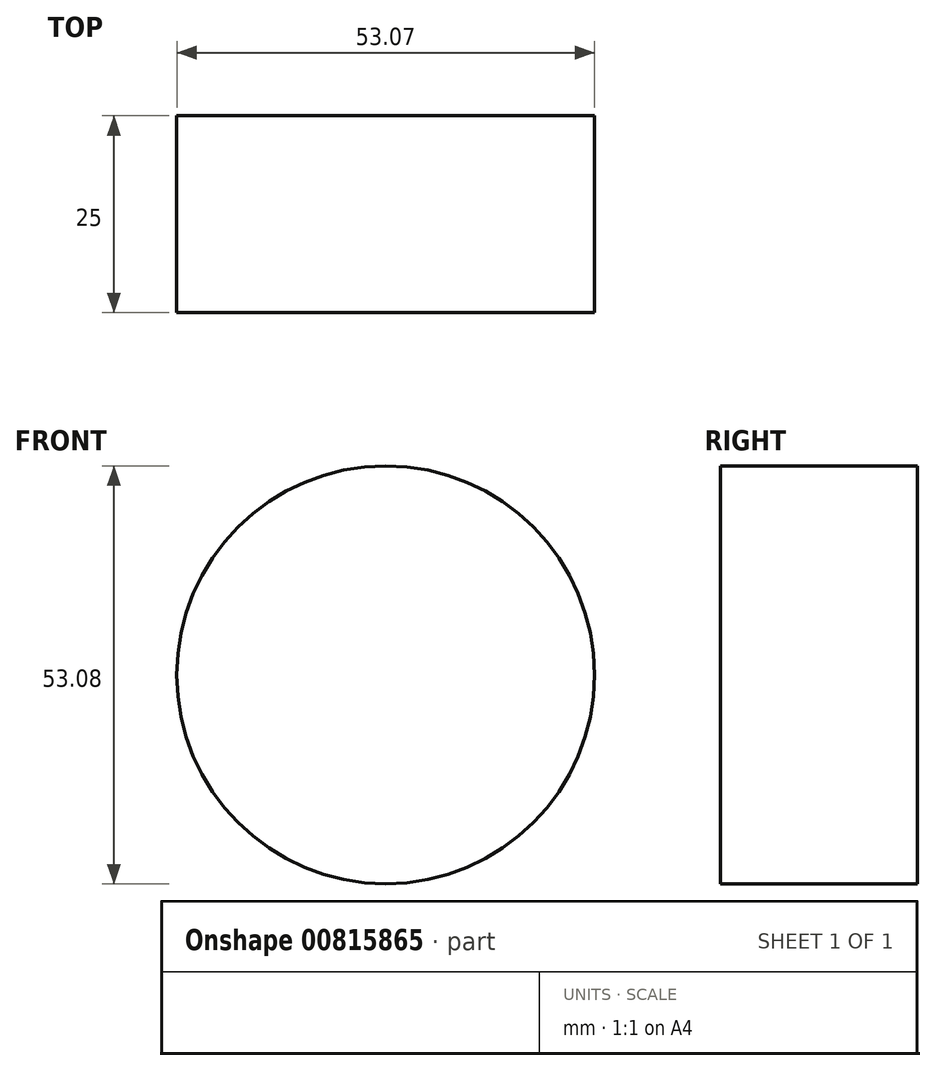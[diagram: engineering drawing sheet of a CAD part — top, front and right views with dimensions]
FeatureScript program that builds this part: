
annotation { "Feature Type Name" : "Feature", "Feature Type Description" : "" }
export const myFeature = defineFeature(function(context is Context, id is Id, definition is map)
    precondition{}
    {
        {
            var Q0;
            Q0=qCreatedBy(makeId("Front.planeOp"),FACE);
            var sketch = newSketch(context, id + "F0", { "sketchPlane" : qUnion([Q0])});
            skLineSegment(sketch, "E0.bottom", {"start": v(-136.5, 52.24) * mm, "end": v(-70.13, 52.24) * mm});
            skLineSegment(sketch, "E0.top", {"start": v(-136.5, 0) * mm, "end": v(-70.13, 0) * mm});
            skLineSegment(sketch, "E0.left", {"start": v(-136.5, 52.24) * mm, "end": v(-136.5, 0) * mm});
            skLineSegment(sketch, "E0.right", {"start": v(-70.13, 52.24) * mm, "end": v(-70.13, 0) * mm});
            skCircle(sketch, "E1", {"center": v(45.03, 64.32) * mm, "radius": 26.54 * mm});
            skSolve(sketch);
        }
        {
            var Q0;
            Q0 = qSketchRegion(id + "F0", true);
            extrude(context, id + "F1", {"entities" : qUnion([Q0]), "depth" : 25 * mm, "offsetDistance" : 25 * mm});
        }
        {
            var Q0;
            Q0=makeQuery(id+"F1.opExtrude","SWEPT_BODY",BODY,{"disambiguationData":[OSD([sQuery(id+"F0.wireOp",EDGE,"E0.bottom"),sQuery(id+"F0.wireOp",EDGE,"E0.top"),sQuery(id+"F0.wireOp",EDGE,"E0.left"),sQuery(id+"F0.wireOp",EDGE,"E0.right")])]});
            deleteBodies(context, id + "F2", {"entities" : qUnion([Q0])});
        }
    });
